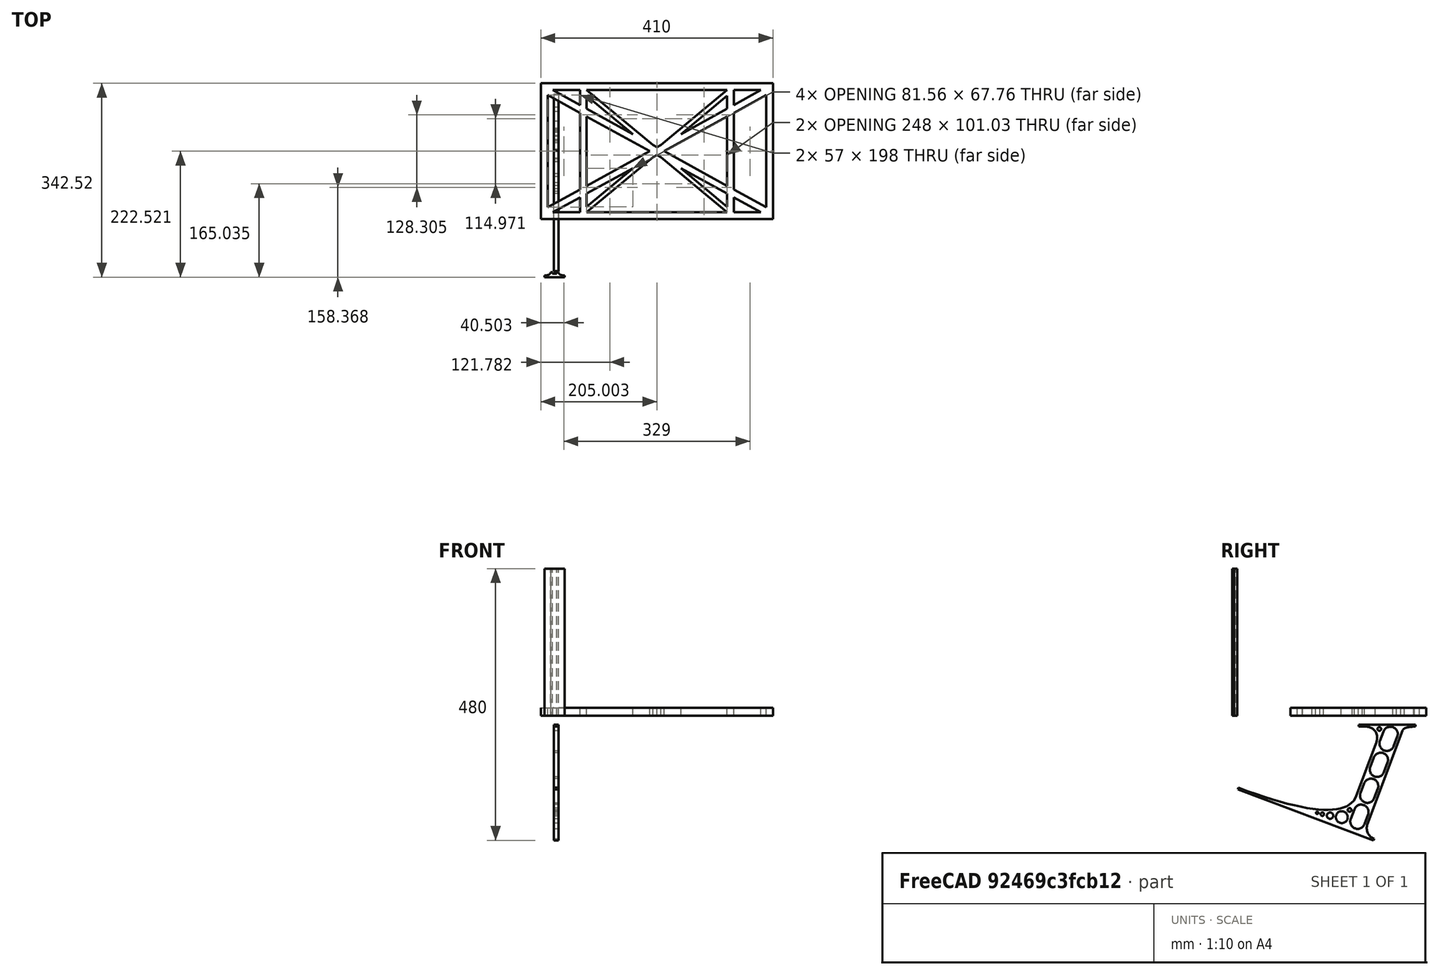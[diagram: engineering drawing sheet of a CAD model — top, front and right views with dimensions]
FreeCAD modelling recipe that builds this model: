
FCSTD DOCUMENT  (FreeCAD 0.19R0.19.2)
Label: laptopStand044
License: All rights reserved
LicenseURL: http://en.wikipedia.org/wiki/All_rights_reserved
objects: Sketcher::SketchObject×3, Part::Extrusion×3
note: 6 computed .brp shape members not serialized (recipe doc carries the construction recipe); baked Part::Feature solids carry a one-line shape summary decoded from their .brp

FEATURE [Sketcher::SketchObject] Sketch
  FullyConstrained = false
  sketch-geometry (62):
    g0: LineSegment StartX=-22.9272 StartY=136.221 StartZ=0 EndX=387.073 EndY=136.221 EndZ=0
    g1: LineSegment StartX=-22.9272 StartY=-103.779 StartZ=0 EndX=387.073 EndY=-103.779 EndZ=0
    g2: LineSegment StartX=375.073 StartY=115.221 StartZ=0 EndX=318.073 EndY=83.9235 EndZ=0
    g3: LineSegment StartX=-10.9272 StartY=-82.7794 StartZ=0 EndX=46.0728 EndY=-51.4823 EndZ=0
    g4: LineSegment StartX=-1.92719 StartY=124.221 StartZ=0 EndX=46.0728 EndY=97.8651 EndZ=0
    g5: LineSegment StartX=366.073 StartY=-91.7794 StartZ=0 EndX=318.073 EndY=-65.424 EndZ=0
    g6: LineSegment StartX=-10.9272 StartY=115.221 StartZ=0 EndX=-10.9272 EndY=-82.7794 EndZ=0
    g7: LineSegment StartX=375.073 StartY=-82.7794 StartZ=0 EndX=375.073 EndY=115.221 EndZ=0
    g8: LineSegment StartX=-1.92719 StartY=-91.7794 StartZ=0 EndX=46.0728 EndY=-91.7794 EndZ=0
    g9: LineSegment StartX=318.073 StartY=124.221 StartZ=0 EndX=366.073 EndY=124.221 EndZ=0
    g10: LineSegment StartX=306.073 StartY=-81.8102 StartZ=0 EndX=224.513 EndY=-14.0532 EndZ=0
    g11: LineSegment StartX=58.0728 StartY=114.251 StartZ=0 EndX=139.632 EndY=46.4944 EndZ=0
    g12: LineSegment StartX=306.073 StartY=124.221 StartZ=0 EndX=189.124 EndY=27.0628 EndZ=0
    g13: LineSegment StartX=58.0728 StartY=-91.7794 StartZ=0 EndX=175.022 EndY=5.37834 EndZ=0
    g14: LineSegment StartX=46.0728 StartY=124.221 StartZ=0 EndX=46.0728 EndY=97.8651 EndZ=0
    g15: LineSegment StartX=58.0728 StartY=-81.8102 StartZ=0 EndX=58.0728 EndY=-58.8351 EndZ=0
    g16: LineSegment StartX=318.073 StartY=124.221 StartZ=0 EndX=318.073 EndY=97.8651 EndZ=0
    g17: LineSegment StartX=306.073 StartY=114.251 StartZ=0 EndX=306.073 EndY=91.2763 EndZ=0
    g18: LineSegment StartX=182.073 StartY=23.1914 StartZ=0 EndX=189.124 EndY=27.0628 EndZ=0
    g19: LineSegment StartX=182.073 StartY=9.24976 StartZ=0 EndX=175.022 EndY=5.37834 EndZ=0
    g20: LineSegment StartX=224.513 StartY=46.4944 StartZ=0 EndX=306.073 EndY=114.251 EndZ=0
    g21: LineSegment StartX=175.022 StartY=27.0628 StartZ=0 EndX=58.0728 EndY=124.221 EndZ=0
    g22: LineSegment StartX=169.377 StartY=16.2206 StartZ=0 EndX=58.0728 EndY=77.3346 EndZ=0
    g23: LineSegment StartX=139.632 StartY=-14.0532 StartZ=0 EndX=58.0728 EndY=-81.8102 EndZ=0
    g24: LineSegment StartX=194.768 StartY=16.2206 StartZ=0 EndX=306.073 EndY=-44.8935 EndZ=0
    g25: LineSegment StartX=224.513 StartY=46.4944 StartZ=0 EndX=306.073 EndY=91.2763 EndZ=0
    g26: LineSegment StartX=175.022 StartY=27.0628 StartZ=0 EndX=179.022 EndY=24.8665 EndZ=0
    g27: LineSegment StartX=139.632 StartY=-14.0532 StartZ=0 EndX=58.0728 EndY=-58.8351 EndZ=0
    g28: LineSegment StartX=189.124 StartY=5.37834 StartZ=0 EndX=185.124 EndY=7.57463 EndZ=0
    g29: LineSegment StartX=189.124 StartY=5.37834 StartZ=0 EndX=306.073 EndY=-91.7794 EndZ=0
    g30: LineSegment StartX=306.073 StartY=77.3346 StartZ=0 EndX=306.073 EndY=-44.8935 EndZ=0
    g31: LineSegment StartX=318.073 StartY=83.9235 StartZ=0 EndX=318.073 EndY=-51.4823 EndZ=0
    g32: LineSegment StartX=318.073 StartY=97.8651 StartZ=0 EndX=366.073 EndY=124.221 EndZ=0
    g33: LineSegment StartX=306.073 StartY=77.3346 StartZ=0 EndX=194.768 EndY=16.2206 EndZ=0
    g34: LineSegment StartX=306.073 StartY=-58.8351 StartZ=0 EndX=224.513 EndY=-14.0532 EndZ=0
    g35: LineSegment StartX=306.073 StartY=-58.8351 StartZ=0 EndX=306.073 EndY=-81.8102 EndZ=0
    g36: LineSegment StartX=318.073 StartY=-51.4823 StartZ=0 EndX=375.073 EndY=-82.7794 EndZ=0
    g37: LineSegment StartX=318.073 StartY=-65.424 StartZ=0 EndX=318.073 EndY=-91.7794 EndZ=0
    g38: LineSegment StartX=306.073 StartY=124.221 StartZ=0 EndX=58.0728 EndY=124.221 EndZ=0
    g39: LineSegment StartX=318.073 StartY=-91.7794 StartZ=0 EndX=366.073 EndY=-91.7794 EndZ=0
    g40: LineSegment StartX=58.0728 StartY=-91.7794 StartZ=0 EndX=306.073 EndY=-91.7794 EndZ=0
    g41: LineSegment StartX=58.0728 StartY=-44.8935 StartZ=0 EndX=58.0728 EndY=77.3346 EndZ=0
    g42: LineSegment StartX=46.0728 StartY=-65.424 StartZ=0 EndX=-1.92719 EndY=-91.7794 EndZ=0
    g43: LineSegment StartX=46.0728 StartY=-65.424 StartZ=0 EndX=46.0728 EndY=-91.7794 EndZ=0
    g44: LineSegment StartX=58.0728 StartY=-44.8935 StartZ=0 EndX=169.377 EndY=16.2206 EndZ=0
    g45: LineSegment StartX=58.0728 StartY=91.2763 StartZ=0 EndX=58.0728 EndY=114.251 EndZ=0
    g46: LineSegment StartX=46.0728 StartY=83.9235 StartZ=0 EndX=46.0728 EndY=-51.4823 EndZ=0
    g47: LineSegment StartX=46.0728 StartY=124.221 StartZ=0 EndX=-1.92719 EndY=124.221 EndZ=0
    g48: LineSegment StartX=58.0728 StartY=91.2763 StartZ=0 EndX=139.632 EndY=46.4944 EndZ=0
    g49: LineSegment StartX=46.0728 StartY=83.9235 StartZ=0 EndX=-10.9272 EndY=115.221 EndZ=0
    g50: LineSegment StartX=-22.9272 StartY=136.221 StartZ=0 EndX=-42.9272 EndY=136.221 EndZ=0
    g51: LineSegment StartX=387.073 StartY=136.221 StartZ=0 EndX=407.073 EndY=136.221 EndZ=0
    g52: LineSegment StartX=-42.9272 StartY=136.221 StartZ=0 EndX=-42.9272 EndY=-103.779 EndZ=0
    g53: LineSegment StartX=-22.9272 StartY=-103.779 StartZ=0 EndX=-42.9272 EndY=-103.779 EndZ=0
    g54: LineSegment StartX=407.073 StartY=136.221 StartZ=0 EndX=407.073 EndY=-103.779 EndZ=0
    g55: LineSegment StartX=387.073 StartY=-103.779 StartZ=0 EndX=407.073 EndY=-103.779 EndZ=0
    g56: LineSegment StartX=179.022 StartY=27.0628 StartZ=0 EndX=179.022 EndY=124.221 EndZ=0
    g57: LineSegment StartX=185.124 StartY=27.0628 StartZ=0 EndX=185.124 EndY=124.221 EndZ=0
    g58: LineSegment StartX=179.022 StartY=27.0628 StartZ=0 EndX=179.022 EndY=24.8665 EndZ=0
    g59: LineSegment StartX=185.124 StartY=27.0628 StartZ=0 EndX=185.124 EndY=24.8665 EndZ=0
    g60: LineSegment StartX=185.124 StartY=7.57463 StartZ=0 EndX=185.124 EndY=-91.7794 EndZ=0
    g61: LineSegment StartX=179.022 StartY=7.57463 StartZ=0 EndX=179.022 EndY=-91.7794 EndZ=0
  constraints (129):
    c: Horizontal(g0)
    c: Distance(g0) = 410
    c: Horizontal(g1)
    c: Block(g0)
    c: Horizontal(g8)
    c: Horizontal(g9)
    c: PointOnObject(g33,g4)
    c: Tangent(g5,g22)
    c: PointOnObject(g22,g3)
    c: PointOnObject(g24,g2)
    c: Coincident(g18,g12)
    c: Tangent(g18,g25)
    c: Coincident(g48,g11)
    c: Coincident(g26,g21)
    c: Coincident(g20,g25)
    c: Coincident(g19,g13)
    c: Coincident(g27,g23)
    c: Tangent(g19,g27)
    c: Coincident(g34,g10)
    c: Coincident(g29,g28)
    c: Coincident(g20,g17)
    c: Tangent(g17,g30)
    c: Tangent(g16,g31)
    c: Coincident(g25,g17)
    c: Tangent(g25,g32)
    c: Coincident(g2,g31)
    c: Coincident(g33,g30)
    c: Tangent(g2,g33)
    c: Coincident(g35,g10)
    c: Tangent(g5,g34)
    c: Tangent(g30,g35)
    c: Coincident(g24,g30)
    c: Tangent(g24,g36)
    c: Coincident(g31,g36)
    c: Coincident(g37,g5)
    c: Tangent(g31,g37)
    c: Coincident(g23,g15)
    c: Tangent(g15,g41)
    c: Coincident(g27,g15)
    c: Tangent(g27,g42)
    c: Coincident(g43,g42)
    c: Tangent(g14,g43)
    c: Coincident(g3,g46)
    c: Coincident(g44,g41)
    c: Tangent(g3,g44)
    c: Tangent(g41,g45)
    c: Tangent(g14,g46)
    c: Coincident(g11,g45)
    c: PointOnObject(g38,g21)
    c: Tangent(g38,g47)
    c: Coincident(g4,g14)
    c: Coincident(g48,g45)
    c: Tangent(g4,g48)
    c: Coincident(g22,g41)
    c: Coincident(g49,g46)
    c: Tangent(g22,g49)
    c: Block(g21)
    c: Block(g12)
    c: Block(g18)
    c: Block(g38)
    c: Block(g16)
    c: Block(g32)
    c: Block(g2)
    c: Block(g36)
    c: Block(g7)
    c: Block(g34)
    c: Block(g35)
    c: Block(g5)
    c: Block(g37)
    c: Block(g20)
    c: Block(g29)
    c: Block(g40)
    c: Block(g19)
    c: Block(g13)
    c: Block(g27)
    c: Block(g23)
    c: Block(g43)
    c: Block(g42)
    c: Block(g3)
    c: Block(g6)
    c: Block(g49)
    c: Block(g4)
    c: Block(g14)
    c: Block(g11)
    c: Block(g45)
    c: Block(g33)
    c: Block(g30)
    c: Block(g22)
    c: Block(g44)
    c: Block(g47)
    c: Block(g9)
    c: Block(g39)
    c: Block(g8)
    c: Horizontal(g50)
    c: Distance(g50) = 20
    c: Coincident(g51,g0)
    c: Horizontal(g51)
    c: Distance(g51) = 20
    c: Coincident(g52,g50)
    c: Vertical(g52)
    c: Horizontal(g53)
    c: Coincident(g53,g52)
    c: Coincident(g54,g51)
    c: Vertical(g54)
    c: Coincident(g55,g1)
    c: Horizontal(g55)
    c: Coincident(g55,g54)
    c: Block(g54)
    c: Block(g53)
    c: Block(g52)
    c: Block(g1)
    c: Vertical(g56)
    c: Vertical(g57)
    c: Vertical(g58)
    c: Vertical(g59)
    c: PointOnObject(g57,g38)
    c: PointOnObject(g56,g38)
    c: PointOnObject(g59,g18)
    c: Tangent(g59,g60)
    c: PointOnObject(g60,g40)
    c: PointOnObject(g61,g40)
    c: PointOnObject(g61,g19)
    c: Tangent(g58,g61)
    c: Coincident(g26,g58)
    c: Coincident(g28,g60)
    c: Block(g56)
    c: Block(g57)
    c: Block(g61)
    c: Block(g60)
FEATURE [Sketcher::SketchObject] Sketch001
  FullyConstrained = true
  MapMode = 4
  Placement = pos=(0,0,0) rot=(0.57735,0.57735,0.57735;2.0944rad)
  Support = -> [Sketch]
  sketch-geometry (46):
    g0: BSplineCurve PolesCount=3 KnotsCount=2 Degree=2 IsPeriodic=0
    g1: ArcOfCircle CenterX=73.122 CenterY=-32.2909 CenterZ=0 NormalX=0 NormalY=0 NormalZ=1 AngleXU=0 Radius=13 StartAngle=5.92268 EndAngle=9.06428
    g2: ArcOfCircle CenterX=66.7816 CenterY=-49.1439 CenterZ=0 NormalX=0 NormalY=0 NormalZ=1 AngleXU=0 Radius=13 StartAngle=2.78068 EndAngle=5.92131
    g3: ArcOfCircle CenterX=55.9263 CenterY=-78.1807 CenterZ=0 NormalX=0 NormalY=0 NormalZ=1 AngleXU=0 Radius=13 StartAngle=5.92268 EndAngle=9.06428
    g4: ArcOfCircle CenterX=49.5884 CenterY=-95.0342 CenterZ=0 NormalX=0 NormalY=0 NormalZ=1 AngleXU=0 Radius=13 StartAngle=2.78068 EndAngle=5.92131
    g5: ArcOfCircle CenterX=38.7206 CenterY=-124.067 CenterZ=0 NormalX=0 NormalY=0 NormalZ=1 AngleXU=0 Radius=13 StartAngle=5.92268 EndAngle=9.06428
    g6: ArcOfCircle CenterX=32.3875 CenterY=-140.92 CenterZ=0 NormalX=0 NormalY=0 NormalZ=1 AngleXU=0 Radius=13 StartAngle=2.78068 EndAngle=5.92131
    g7: ArcOfCircle CenterX=21.4715 CenterY=-169.934 CenterZ=0 NormalX=0 NormalY=0 NormalZ=1 AngleXU=0 Radius=13 StartAngle=5.92268 EndAngle=9.06428
    g8: ArcOfCircle CenterX=15.1336 CenterY=-186.787 CenterZ=0 NormalX=0 NormalY=0 NormalZ=1 AngleXU=0 Radius=13 StartAngle=2.78068 EndAngle=5.92131
    g9-g12: Circle x4 (B-spline internal-alignment scaffolding for g13; pole/knot coordinates omitted)
    g13: BSplineCurve PolesCount=4 KnotsCount=2 Degree=3 IsPeriodic=0
    g14: GeomPoint X=28.8094 Y=-19.0875 Z=0
    g15: GeomPoint X=47.0443 Y=-50.4712 Z=0
    g16: Circle CenterX=53.5586 CenterY=-23.2695 CenterZ=0 NormalX=0 NormalY=0 NormalZ=1 AngleXU=0 Radius=3.24518
    g17: Circle CenterX=-195.441 CenterY=-127.082 CenterZ=0 NormalX=0 NormalY=0 NormalZ=1 AngleXU=0 Radius=1
    g18: Circle CenterX=-8.24091 CenterY=-197.481 CenterZ=0 NormalX=0 NormalY=0 NormalZ=1 AngleXU=0 Radius=1
    g19: Circle CenterX=12.8789 CenterY=-141.321 CenterZ=0 NormalX=0 NormalY=0 NormalZ=1 AngleXU=0 Radius=1
    g20: BSplineCurve PolesCount=3 KnotsCount=2 Degree=2 IsPeriodic=0
    g21: GeomPoint X=-195.441 Y=-127.082 Z=0
    g22: GeomPoint X=12.8789 Y=-141.321 Z=0
    g23: Circle CenterX=-12.8016 CenterY=-179.036 CenterZ=0 NormalX=0 NormalY=0 NormalZ=1 AngleXU=0 Radius=10.5072
    g24: Circle CenterX=0.933922 CenterY=-166.43 CenterZ=0 NormalX=0 NormalY=0 NormalZ=1 AngleXU=0 Radius=3.26661
    g25: Circle CenterX=-33.5518 CenterY=-176.44 CenterZ=0 NormalX=0 NormalY=0 NormalZ=1 AngleXU=0 Radius=5.64388
    g26: Circle CenterX=-47.2366 CenterY=-173.859 CenterZ=0 NormalX=0 NormalY=0 NormalZ=1 AngleXU=0 Radius=3.01653
    g27: Circle CenterX=-56.2595 CenterY=-171.456 CenterZ=0 NormalX=0 NormalY=0 NormalZ=1 AngleXU=0 Radius=2.12826
    g28: ArcOfCircle CenterX=51.2151 CenterY=-198.473 CenterZ=0 NormalX=0 NormalY=0 NormalZ=1 AngleXU=0 Radius=20 StartAngle=2.78189 EndAngle=4.35269
    g29: LineSegment StartX=32.4951 StartY=-191.433 StartZ=0 EndX=94.6577 EndY=-26.1351 EndZ=0
    g30: LineSegment StartX=43.1192 StartY=-220.001 StartZ=0 EndX=-196.497 EndY=-129.89 EndZ=0
    g31: LineSegment StartX=43.1192 StartY=-220.001 StartZ=0 EndX=44.1752 EndY=-217.193 EndZ=0
    g32: LineSegment StartX=117.223 StartY=-19.0875 StartZ=0 EndX=117.223 EndY=-16.0875 EndZ=0
    g33: LineSegment StartX=117.223 StartY=-16.0875 StartZ=0 EndX=17.2232 EndY=-16.0875 EndZ=0
    g34: LineSegment StartX=17.2232 StartY=-16.0875 StartZ=0 EndX=17.2232 EndY=-19.0875 EndZ=0
    g35: LineSegment StartX=28.8094 StartY=-19.0875 StartZ=0 EndX=17.2232 EndY=-19.0875 EndZ=0
    g36: LineSegment StartX=47.0443 StartY=-50.4712 StartZ=0 EndX=12.8789 EndY=-141.321 EndZ=0
    g37: LineSegment StartX=-195.441 StartY=-127.082 StartZ=0 EndX=-196.497 EndY=-129.89 EndZ=0
    g38: LineSegment StartX=85.2864 StartY=-36.8765 StartZ=0 EndX=78.9396 EndY=-53.7463 EndZ=0
    g39: LineSegment StartX=60.9577 StartY=-27.7052 StartZ=0 EndX=54.6191 EndY=-44.5532 EndZ=0
    g40: LineSegment StartX=68.0907 StartY=-82.7664 StartZ=0 EndX=61.7465 EndY=-99.6365 EndZ=0
    g41: LineSegment StartX=43.7619 StartY=-73.595 StartZ=0 EndX=37.426 EndY=-90.4435 EndZ=0
    g42: LineSegment StartX=50.885 StartY=-128.652 StartZ=0 EndX=44.5456 EndY=-145.522 EndZ=0
    g43: LineSegment StartX=26.5562 StartY=-119.481 StartZ=0 EndX=20.2251 EndY=-136.329 EndZ=0
    g44: LineSegment StartX=9.3071 StartY=-165.349 StartZ=0 EndX=2.97115 EndY=-182.197 EndZ=0
    g45: LineSegment StartX=33.6358 StartY=-174.52 StartZ=0 EndX=27.2917 EndY=-191.39 EndZ=0
  constraints (70):
    c: Block(g0)
    c: Block(g1)
    c: Block(g2)
    c: Block(g4)
    c: Block(g3)
    c: Block(g6)
    c: Block(g5)
    c: Block(g8)
    c: Block(g7)
    c: Weight(g9) = 1
    c: Equal(g9,g10)
    c: Equal(g9,g11)
    c: Equal(g9,g12)
    c: InternalAlignment(g9-g12 -> g13) x4
    c: InternalAlignment(g14,g13)
    c: InternalAlignment(g15,g13)
    c: Block(g16)
    c: Weight(g17) = 1
    c: Equal(g17,g18)
    c: Equal(g17,g19)
    c: InternalAlignment(g17,g20)
    c: InternalAlignment(g18,g20)
    c: InternalAlignment(g19,g20)
    c: InternalAlignment(g21,g20)
    c: InternalAlignment(g22,g20)
    c: Block(g20)
    c: Block(g23)
    c: Block(g24)
    c: Block(g25)
    c: Block(g26)
    c: Block(g27)
    c: Block(g28)
    c: Coincident(g29,g28)
    c: Coincident(g29,g0)
    c: Block(g13)
    c: Coincident(g31,g30)
    c: Coincident(g31,g28)
    c: Block(g31)
    c: Coincident(g32,g0)
    c: Vertical(g32)
    c: Coincident(g33,g32)
    c: Horizontal(g33)
    c: Coincident(g34,g33)
    c: Vertical(g34)
    c: Block(g33)
    c: Coincident(g35,g13)
    c: Coincident(g35,g34)
    c: Horizontal(g35)
    c: Coincident(g36,g13)
    c: Coincident(g36,g20)
    c: Coincident(g37,g20)
    c: Coincident(g37,g30)
    c: Block(g30)
    c: Coincident(g38,g1)
    c: Coincident(g38,g2)
    c: Coincident(g39,g1)
    c: Coincident(g39,g2)
    c: Coincident(g40,g3)
    c: Coincident(g40,g4)
    c: Coincident(g41,g3)
    c: Coincident(g41,g4)
    c: Coincident(g42,g5)
    c: Coincident(g42,g6)
    c: Coincident(g43,g5)
    c: Coincident(g43,g6)
    c: Coincident(g44,g7)
    c: Coincident(g44,g8)
    c: Coincident(g45,g7)
    c: Coincident(g45,g8)
    c: Distance(g30) = 256
FEATURE [Part::Extrusion] Extrude002
  Base = -> Sketch001
  Dir = (1,0,0)
  DirMode = 2
  FaceMakerClass = Part::FaceMakerBullseye
  LengthFwd = 8
  LengthRev = 0
  Solid = true
  Symmetric = false
FEATURE [Sketcher::SketchObject] Sketch002
  FullyConstrained = true
  sketch-geometry (20):
    g0: LineSegment StartX=-2.77179 StartY=-200.304 StartZ=0 EndX=5.22821 EndY=-200.304 EndZ=0
    g1: LineSegment StartX=5.22821 StartY=-200.304 StartZ=0 EndX=5.22821 EndY=-197.304 EndZ=0
    g2: LineSegment StartX=-2.77179 StartY=-200.304 StartZ=0 EndX=-2.77179 EndY=-197.304 EndZ=0
    g3: LineSegment StartX=5.22821 StartY=-197.304 StartZ=0 EndX=8.22821 EndY=-197.304 EndZ=0
    g4: LineSegment StartX=-2.77179 StartY=-197.304 StartZ=0 EndX=-5.77179 EndY=-197.304 EndZ=0
    g5: LineSegment StartX=19.2282 StartY=-203.304 StartZ=0 EndX=19.2282 EndY=-206.304 EndZ=0
    g6: LineSegment StartX=-16.7718 StartY=-203.304 StartZ=0 EndX=-16.7718 EndY=-206.304 EndZ=0
    g7: LineSegment StartX=-16.7718 StartY=-206.304 StartZ=0 EndX=19.2282 EndY=-206.304 EndZ=0
    g8: Circle CenterX=-16.7718 CenterY=-203.304 CenterZ=0 NormalX=0 NormalY=0 NormalZ=1 AngleXU=0 Radius=1
    g9: Circle CenterX=-5.77179 CenterY=-203.304 CenterZ=0 NormalX=0 NormalY=0 NormalZ=1 AngleXU=0 Radius=1
    g10: Circle CenterX=-5.77179 CenterY=-197.304 CenterZ=0 NormalX=0 NormalY=0 NormalZ=1 AngleXU=0 Radius=1
    g11: BSplineCurve PolesCount=3 KnotsCount=2 Degree=2 IsPeriodic=0
    g12: GeomPoint X=-16.7718 Y=-203.304 Z=0
    g13: GeomPoint X=-5.77179 Y=-197.304 Z=0
    g14: Circle CenterX=19.2282 CenterY=-203.304 CenterZ=0 NormalX=0 NormalY=0 NormalZ=1 AngleXU=0 Radius=1
    g15: Circle CenterX=8.22821 CenterY=-203.304 CenterZ=0 NormalX=0 NormalY=0 NormalZ=1 AngleXU=0 Radius=1
    g16: Circle CenterX=8.22821 CenterY=-197.304 CenterZ=0 NormalX=0 NormalY=0 NormalZ=1 AngleXU=0 Radius=1
    g17: BSplineCurve PolesCount=3 KnotsCount=2 Degree=2 IsPeriodic=0
    g18: GeomPoint X=19.2282 Y=-203.304 Z=0
    g19: GeomPoint X=8.22821 Y=-197.304 Z=0
  constraints (41):
    c: Horizontal(g0)
    c: Distance(g0) = 8
    c: Coincident(g1,g0)
    c: Vertical(g1)
    c: Distance(g1) = 3
    c: Coincident(g2,g0)
    c: Vertical(g2)
    c: Distance(g2) = 3
    c: Coincident(g3,g1)
    c: Horizontal(g3)
    c: Distance(g3) = 3
    c: Coincident(g4,g2)
    c: Horizontal(g4)
    c: Distance(g4) = 3
    c: Vertical(g5)
    c: Vertical(g6)
    c: Coincident(g7,g6)
    c: Coincident(g7,g5)
    c: Weight(g8) = 1
    c: Equal(g8,g9)
    c: Equal(g8,g10)
    c: Coincident(g11,g4)
    c: InternalAlignment(g8,g11)
    c: InternalAlignment(g9,g11)
    c: InternalAlignment(g10,g11)
    c: InternalAlignment(g12,g11)
    c: InternalAlignment(g13,g11)
    c: Coincident(g17,g5)
    c: Weight(g14) = 1
    c: Equal(g14,g15)
    c: Equal(g14,g16)
    c: Coincident(g17,g3)
    c: InternalAlignment(g14,g17)
    c: InternalAlignment(g15,g17)
    c: InternalAlignment(g16,g17)
    c: InternalAlignment(g18,g17)
    c: InternalAlignment(g19,g17)
    c: Block(g7)
    c: Block(g17)
    c: Block(g11)
    c: Block(g6)
FEATURE [Part::Extrusion] Extrude003
  Base = -> Sketch002
  Dir = (0,0,1)
  DirMode = 2
  FaceMakerClass = Part::FaceMakerBullseye
  LengthFwd = 260
  LengthRev = 0
  Solid = true
  Symmetric = false
FEATURE [Part::Extrusion] Extrude
  Base = -> Sketch
  Dir = (0,0,1)
  DirMode = 2
  FaceMakerClass = Part::FaceMakerBullseye
  LengthFwd = 14
  LengthRev = 0
  Solid = true
  Symmetric = false
